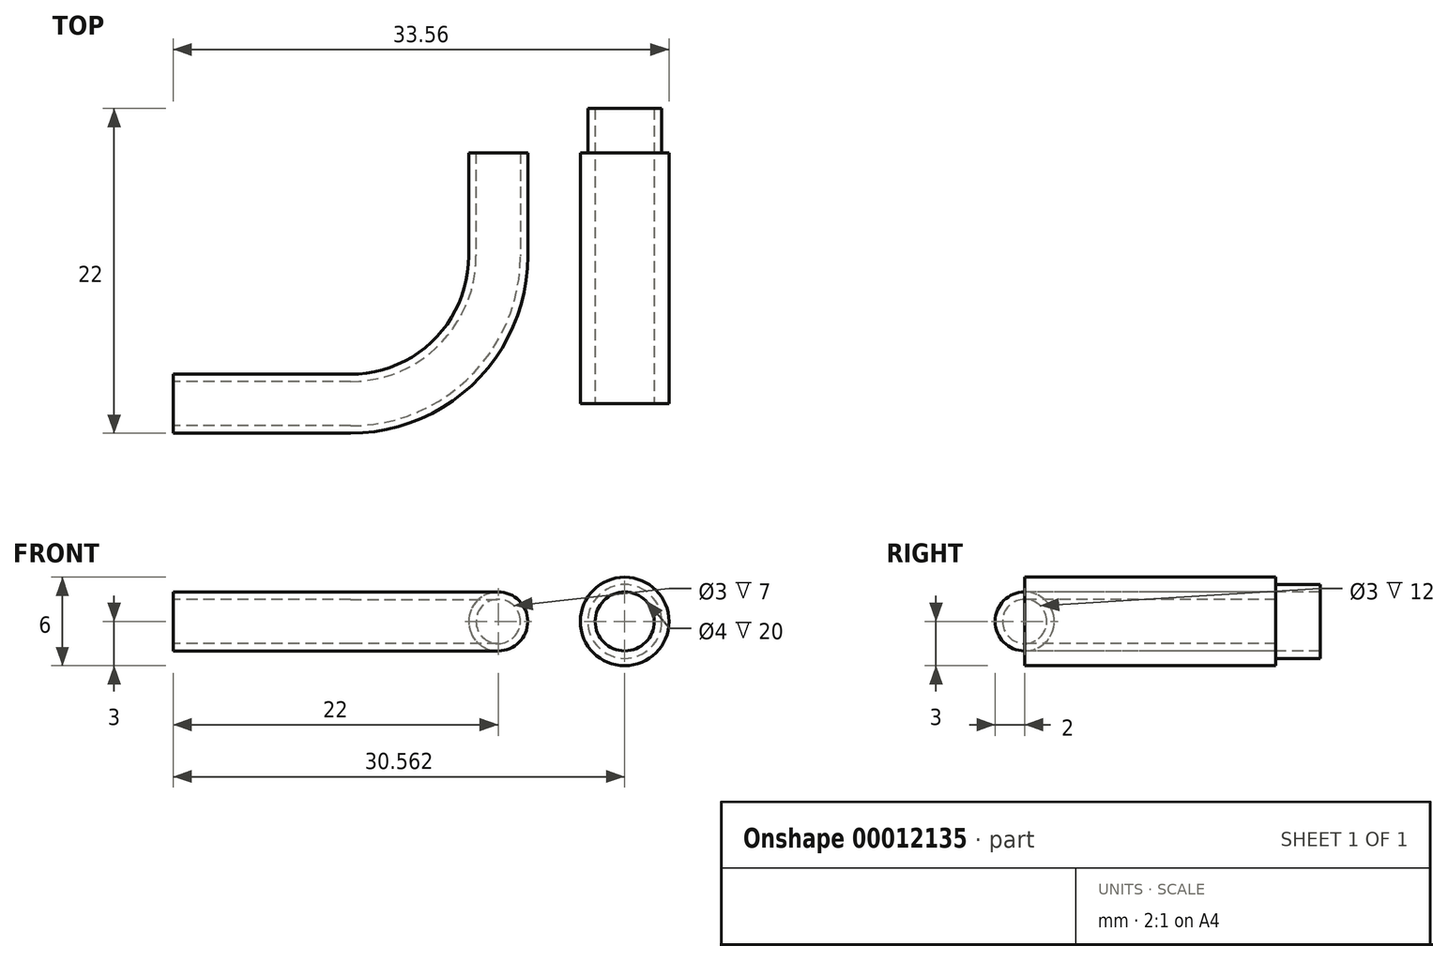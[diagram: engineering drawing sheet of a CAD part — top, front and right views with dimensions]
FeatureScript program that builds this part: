
annotation { "Feature Type Name" : "Feature", "Feature Type Description" : "" }
export const myFeature = defineFeature(function(context is Context, id is Id, definition is map)
    precondition{}
    {
        {
            var Q0;
            Q0=qCreatedBy(makeId("Front.planeOp"),FACE);
            var sketch = newSketch(context, id + "F0", { "sketchPlane" : qUnion([Q0])});
            skCircle(sketch, "E0", {"center": v(0, 0) * mm, "radius": 1.5 * mm});
            skCircle(sketch, "E1", {"center": v(0, 0) * mm, "radius": 2 * mm});
            skSolve(sketch);
        }
        {
            var Q0;
            Q0=qCreatedBy(makeId("Top.planeOp"),FACE);
            var sketch = newSketch(context, id + "F1", { "sketchPlane" : qUnion([Q0])});
            skLineSegment(sketch, "E2", {"start": v(0, 0) * mm, "end": v(0, -7) * mm});
            skLineSegment(sketch, "E3", {"start": v(-10, -17) * mm, "end": v(-22, -17) * mm});
            skPoint(sketch, "E4.visualSharp", {"position": v(0, -17) * mm});
            skArc(sketch, "E4.filletArc", {"start": v(-10, -17) * mm, "mid": v(-2.93, -14.07) * mm, "end": v(0, -7) * mm});
            skSolve(sketch);
        }
        {
            var Q0;
            Q0=makeQuery(id+"F0.imprint","IMPRINT",FACE,{"disambiguationData":[TD([[makeQuery(id+"F0.imprint","IMPRINT",EDGE,{"derivedFrom":sQuery(id+"F0.wireOp",EDGE,"E0")}),-1.0]])]});
            var Q1;
            Q1=sQuery(id+"F1.wireOp",EDGE,"E4.filletArc");
            var Q2;
            Q2=sQuery(id+"F1.wireOp",EDGE,"E2");
            var Q3;
            Q3=sQuery(id+"F1.wireOp",EDGE,"E3");
            sweep(context, id + "F2", {"profiles" : qUnion([Q0]), "path" : qUnion([Q1, Q2, Q3])});
        }
        {
            var Q0;
            Q0=qCreatedBy(makeId("Front.planeOp"),FACE);
            var sketch = newSketch(context, id + "F3", { "sketchPlane" : qUnion([Q0])});
            skCircle(sketch, "E5", {"center": v(8.56, 0) * mm, "radius": 2 * mm});
            skCircle(sketch, "E6", {"center": v(8.56, 0) * mm, "radius": 2.5 * mm});
            skCircle(sketch, "E7", {"center": v(8.56, 0) * mm, "radius": 3 * mm});
            skSolve(sketch);
        }
        {
            var Q0;
            Q0=makeQuery(id+"F3.imprint","IMPRINT",FACE,{"disambiguationData":[TD([[makeQuery(id+"F3.imprint","IMPRINT",EDGE,{"derivedFrom":sQuery(id+"F3.wireOp",EDGE,"E5")}),-1.0]])]});
            extrude(context, id + "F4", {"entities" : qUnion([Q0]), "oppositeDirection" : true, "depth" : 3 * mm});
        }
        {
            var Q0;
            Q0=makeQuery(id+"F3.imprint","IMPRINT",FACE,{"disambiguationData":[TD([[makeQuery(id+"F3.imprint","IMPRINT",EDGE,{"derivedFrom":sQuery(id+"F3.wireOp",EDGE,"E6")}),-1.0]])]});
            var Q1;
            Q1=makeQuery(id+"F3.imprint","IMPRINT",FACE,{"disambiguationData":[TD([[makeQuery(id+"F3.imprint","IMPRINT",EDGE,{"derivedFrom":sQuery(id+"F3.wireOp",EDGE,"E5")}),-1.0]])]});
            extrude(context, id + "F5", {"entities" : qUnion([Q0, Q1]), "operationType" : NewBodyOperationType.ADD, "depth" : 17 * mm});
        }
    });
